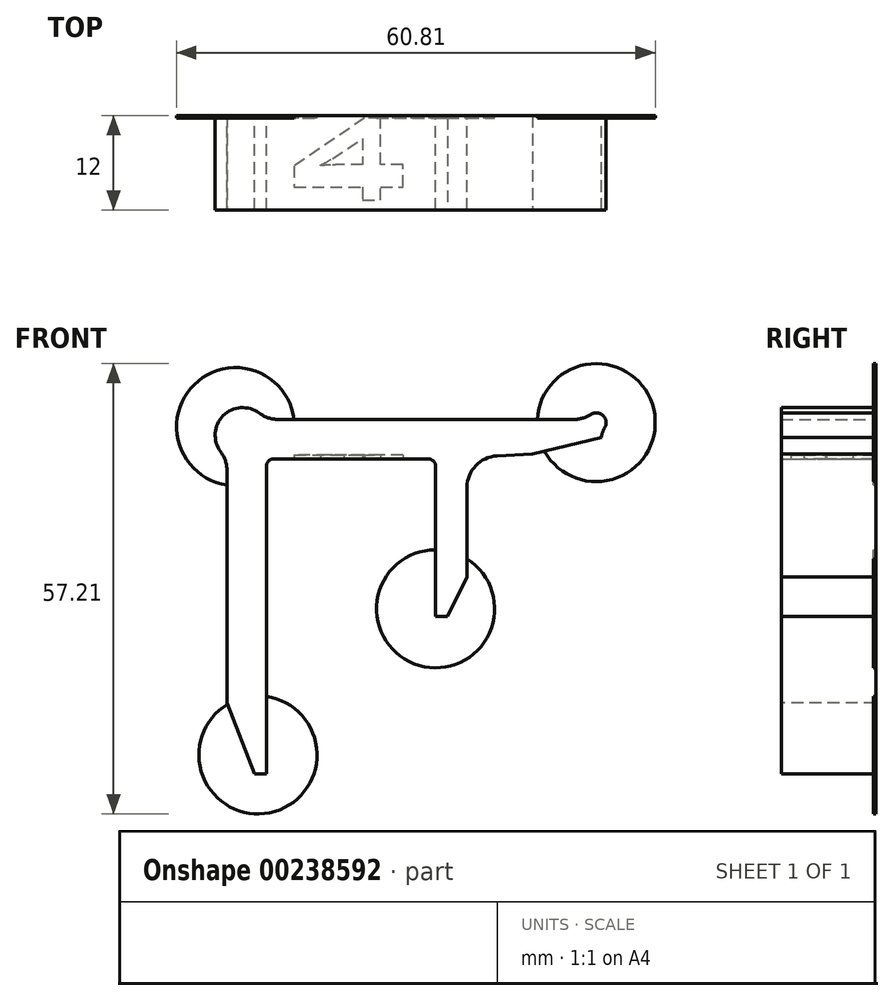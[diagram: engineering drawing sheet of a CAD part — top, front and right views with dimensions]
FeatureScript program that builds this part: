
annotation { "Feature Type Name" : "Feature", "Feature Type Description" : "" }
export const myFeature = defineFeature(function(context is Context, id is Id, definition is map)
    precondition{}
    {
        {
            var Q0;
            Q0=qCreatedBy(makeId("Front.planeOp"),FACE);
            var sketch = newSketch(context, id + "F0", { "sketchPlane" : qUnion([Q0])});
            skLineSegment(sketch, "E0", {"start": v(0, 0) * mm, "end": v(21.5, 0) * mm});
            skLineSegment(sketch, "E1", {"start": v(0, 0) * mm, "end": v(0, -40) * mm});
            skLineSegment(sketch, "E2", {"start": v(0, -40) * mm, "end": v(-5, -40) * mm});
            skLineSegment(sketch, "E3", {"start": v(-5, -40) * mm, "end": v(-5, 5) * mm});
            skLineSegment(sketch, "E4", {"start": v(-5, 5) * mm, "end": v(21.5, 5) * mm});
            skLineSegment(sketch, "E5", {"start": v(21.5, 5) * mm, "end": v(21.5, 0) * mm});
            skLineSegment(sketch, "E6", {"start": v(21.5, 0) * mm, "end": v(42.5, 1) * mm});
            skLineSegment(sketch, "E7", {"start": v(21.5, 0) * mm, "end": v(21.5, -20) * mm});
            skLineSegment(sketch, "E8", {"start": v(21.5, -20) * mm, "end": v(25.5, -20) * mm});
            skLineSegment(sketch, "E9", {"start": v(25.5, -20) * mm, "end": v(25.5, 0.2) * mm});
            skLineSegment(sketch, "E10", {"start": v(21.5, 5) * mm, "end": v(42.5, 5) * mm});
            skLineSegment(sketch, "E11", {"start": v(42.5, 5) * mm, "end": v(42.5, 1) * mm});
            skCircle(sketch, "E12", {"center": v(41.9, 4.6) * mm, "radius": 1.25 * mm});
            skCircle(sketch, "E13", {"center": v(-3, 3) * mm, "radius": 3.5 * mm});
            skSolve(sketch);
        }
        {
            var Q0;
            {var subQ0=sQuery(id+"F0.wireOp",EDGE,"E11");var subQ1=sQuery(id+"F0.wireOp",EDGE,"E10");var subQ2=makeQuery(id+"F0.imprint","INTERSECT",VERTEX,{"derivedFrom":[subQ1,subQ0]});Q0=makeQuery(id+"F0.imprint","IMPRINT",FACE,{"disambiguationData":[TD([[makeQuery(id+"F0.imprint","IMPRINT",EDGE,{"disambiguationData":[TD([[subQ2,1.0]])],"derivedFrom":subQ1}),-1.0]])]});}
            var Q1;
            {var subQ0=sQuery(id+"F0.wireOp",EDGE,"E11");var subQ1=sQuery(id+"F0.wireOp",EDGE,"E10");var subQ2=makeQuery(id+"F0.imprint","INTERSECT",VERTEX,{"derivedFrom":[subQ1,subQ0]});Q1=makeQuery(id+"F0.imprint","IMPRINT",FACE,{"disambiguationData":[TD([[makeQuery(id+"F0.imprint","IMPRINT",EDGE,{"disambiguationData":[TD([[subQ2,1.0]])],"derivedFrom":subQ1}),1.0]])]});}
            var Q2;
            {var subQ1=sQuery(id+"F0.wireOp",EDGE,"E5");Q2=makeQuery(id+"F0.imprint","IMPRINT",FACE,{"disambiguationData":[TD([[makeQuery(id+"F0.imprint","IMPRINT",EDGE,{"derivedFrom":subQ1}),1.0]])]});}
            var Q3;
            {var subQ0=sQuery(id+"F0.wireOp",EDGE,"E7");Q3=makeQuery(id+"F0.imprint","IMPRINT",FACE,{"disambiguationData":[TD([[makeQuery(id+"F0.imprint","IMPRINT",EDGE,{"derivedFrom":subQ0}),1.0]])]});}
            var Q4;
            Q4=makeQuery(id+"F0.imprint","IMPRINT",FACE,{"disambiguationData":[TD([[makeQuery(id+"F0.imprint","IMPRINT",EDGE,{"derivedFrom":sQuery(id+"F0.wireOp",EDGE,"E0")}),1.0]])]});
            var Q5;
            {var subQ0=sQuery(id+"F0.wireOp",EDGE,"E4");var subQ1=sQuery(id+"F0.wireOp",EDGE,"E3");var subQ2=makeQuery(id+"F0.imprint","INTERSECT",VERTEX,{"derivedFrom":[subQ1,subQ0]});Q5=makeQuery(id+"F0.imprint","IMPRINT",FACE,{"disambiguationData":[TD([[makeQuery(id+"F0.imprint","IMPRINT",EDGE,{"disambiguationData":[TD([[subQ2,1.0]])],"derivedFrom":subQ1}),-1.0]])]});}
            var Q6;
            {var subQ0=sQuery(id+"F0.wireOp",EDGE,"E4");var subQ1=sQuery(id+"F0.wireOp",EDGE,"E3");var subQ2=makeQuery(id+"F0.imprint","INTERSECT",VERTEX,{"derivedFrom":[subQ1,subQ0]});Q6=makeQuery(id+"F0.imprint","IMPRINT",FACE,{"disambiguationData":[TD([[makeQuery(id+"F0.imprint","IMPRINT",EDGE,{"disambiguationData":[TD([[subQ2,1.0]])],"derivedFrom":subQ1}),1.0]])]});}
            extrude(context, id + "F1", {"entities" : qUnion([Q0, Q1, Q2, Q3, Q4, Q5, Q6]), "depth" : 12 * mm, "offsetDistance" : 25 * mm, "symmetric" : true});
        }
        {
            var Q0;
            Q0=makeQuery(id+"F1.opExtrude","SWEPT_EDGE",EDGE,{"disambiguationData":[OSD([sQuery(id+"F0.wireOp",EDGE,"E0"),sQuery(id+"F0.wireOp",EDGE,"E1")])]});
            var Q1;
            Q1=makeQuery(id+"F1.opExtrude","SWEPT_EDGE",EDGE,{"disambiguationData":[OSD([sQuery(id+"F0.wireOp",EDGE,"E0"),sQuery(id+"F0.wireOp",EDGE,"E5"),sQuery(id+"F0.wireOp",EDGE,"E6"),sQuery(id+"F0.wireOp",EDGE,"E7")])]});
            fillet(context, id + "F2", {"entities" : qUnion([Q0, Q1]), "radius" : 1 * mm, "tangentPropagation" : true, "allowEdgeOverflow" : false});
        }
        {
            var Q0;
            Q0=makeQuery(id+"F1.opExtrude","SWEPT_EDGE",EDGE,{"disambiguationData":[OSD([sQuery(id+"F0.wireOp",EDGE,"E8"),sQuery(id+"F0.wireOp",EDGE,"E9")])]});
            chamfer(context, id + "F3", {"entities" : qUnion([Q0]), "chamferType" : ChamferType.TWO_OFFSETS, "width1" : 5 * mm, "oppositeDirection" : false, "width2" : 2.5 * mm, "tangentPropagation" : true});
        }
        {
            var Q0;
            Q0=makeQuery(id+"F1.opExtrude","SWEPT_EDGE",EDGE,{"disambiguationData":[OSD([sQuery(id+"F0.wireOp",EDGE,"E6"),sQuery(id+"F0.wireOp",EDGE,"E9")])]});
            var Q1;
            Q1=makeQuery(id+"F1.opExtrude","SWEPT_EDGE",EDGE,{"disambiguationData":[OSD([sQuery(id+"F0.wireOp",EDGE,"E4"),sQuery(id+"F0.wireOp",EDGE,"E13")])]});
            var Q2;
            Q2=makeQuery(id+"F1.opExtrude","SWEPT_EDGE",EDGE,{"disambiguationData":[OSD([sQuery(id+"F0.wireOp",EDGE,"E3"),sQuery(id+"F0.wireOp",EDGE,"E13")])]});
            var Q3;
            Q3=makeQuery(id+"F1.opExtrude","SWEPT_EDGE",EDGE,{"disambiguationData":[OSD([sQuery(id+"F0.wireOp",EDGE,"E10"),sQuery(id+"F0.wireOp",EDGE,"E12")])]});
            var Q4;
            Q4=makeQuery(id+"F1.opExtrude","SWEPT_EDGE",EDGE,{"disambiguationData":[OSD([sQuery(id+"F0.wireOp",EDGE,"E11"),sQuery(id+"F0.wireOp",EDGE,"E12")])]});
            fillet(context, id + "F4", {"entities" : qUnion([Q0, Q1, Q2, Q3, Q4]), "radius" : 4 * mm, "tangentPropagation" : true, "allowEdgeOverflow" : false});
        }
        {
            var Q0;
            Q0=makeQuery(id+"F1.opExtrude","SWEPT_EDGE",EDGE,{"disambiguationData":[OSD([sQuery(id+"F0.wireOp",EDGE,"E2"),sQuery(id+"F0.wireOp",EDGE,"E3")])]});
            var Q1;
            Q1=makeQuery(id+"F1.opExtrude","SWEPT_EDGE",EDGE,{"disambiguationData":[OSD([sQuery(id+"F0.wireOp",EDGE,"E6"),sQuery(id+"F0.wireOp",EDGE,"E11")])]});
            chamfer(context, id + "F5", {"entities" : qUnion([Q0, Q1]), "chamferType" : ChamferType.TWO_OFFSETS, "width1" : 3.5 * mm, "oppositeDirection" : false, "width2" : 9 * mm, "tangentPropagation" : true});
        }
        {
            var Q0;
            Q0=makeQuery(id+"F1.opExtrude","SWEPT_FACE",FACE,{"disambiguationData":[OSD([sQuery(id+"F0.wireOp",EDGE,"E0")])]});
            var sketch = newSketch(context, id + "F6", { "sketchPlane" : qUnion([Q0])});
            skText(sketch, "E14", { "text": "4", "fontName": "OpenSans-Bold.ttf"});
            const initialGuessF6  = {"E14": [0.01736, -0.006, 0, 1, 0.01394]};
            skSetInitialGuess(sketch, initialGuessF6);
            skSolve(sketch);
        }
        {
            var Q0;
            Q0 = qSketchRegion(id + "F6", true);
            extrude(context, id + "F7", {"entities" : qUnion([Q0]), "operationType" : NewBodyOperationType.REMOVE, "oppositeDirection" : true, "depth" : 0.5 * mm, "offsetDistance" : 25 * mm});
        }
        {
            var Q0;
            Q0=makeQuery(id+"F1.opExtrude","CAP_FACE",FACE,{"disambiguationData":[OSD([sQuery(id+"F0.wireOp",EDGE,"E0"),sQuery(id+"F0.wireOp",EDGE,"E1"),sQuery(id+"F0.wireOp",EDGE,"E2"),sQuery(id+"F0.wireOp",EDGE,"E3"),sQuery(id+"F0.wireOp",EDGE,"E4"),sQuery(id+"F0.wireOp",EDGE,"E6"),sQuery(id+"F0.wireOp",EDGE,"E7"),sQuery(id+"F0.wireOp",EDGE,"E8"),sQuery(id+"F0.wireOp",EDGE,"E9"),sQuery(id+"F0.wireOp",EDGE,"E10"),sQuery(id+"F0.wireOp",EDGE,"E11"),sQuery(id+"F0.wireOp",EDGE,"E12"),sQuery(id+"F0.wireOp",EDGE,"E13")])],"isStart":true});
            var sketch = newSketch(context, id + "F8", { "sketchPlane" : qUnion([Q0])});
            skCircle(sketch, "E15", {"center": v(1.06, -37.61) * mm, "radius": 7.5 * mm});
            skCircle(sketch, "E16", {"center": v(-21.5, -19.06) * mm, "radius": 7.5 * mm});
            skCircle(sketch, "E17", {"center": v(-41.9, 4.6) * mm, "radius": 7.5 * mm});
            skCircle(sketch, "E18", {"center": v(3.9, 4.08) * mm, "radius": 7.5 * mm});
            skSolve(sketch);
        }
        {
            var Q0;
            {var subQ0=sQuery(id+"F0.wireOp",EDGE,"E12");Q0=makeQuery(id+"F8.imprint","IMPRINT",FACE,{"disambiguationData":[TD([[makeQuery(id+"F8.imprint","IMPRINT",EDGE,{"derivedFrom":makeQuery(id+"F1.opExtrude","CAP_EDGE",EDGE,{"disambiguationData":[OSD([subQ0])],"isStart":true})}),1.0]])]});}
            var Q1;
            {var subQ0=sQuery(id+"F0.wireOp",EDGE,"E13");Q1=makeQuery(id+"F8.imprint","IMPRINT",FACE,{"disambiguationData":[TD([[makeQuery(id+"F8.imprint","IMPRINT",EDGE,{"derivedFrom":makeQuery(id+"F1.opExtrude","CAP_EDGE",EDGE,{"disambiguationData":[OSD([subQ0])],"isStart":true})}),1.0]])]});}
            var Q2;
            {var subQ5=sQuery(id+"F0.wireOp",EDGE,"E8");var subQ8=makeQuery(id+"F1.opExtrude","CAP_EDGE",EDGE,{"disambiguationData":[OSD([subQ5])],"isStart":true});Q2=makeQuery(id+"F8.imprint","IMPRINT",FACE,{"disambiguationData":[TD([[makeQuery(id+"F8.imprint","IMPRINT",EDGE,{"derivedFrom":subQ8}),1.0]])]});}
            var Q3;
            {var subQ5=sQuery(id+"F0.wireOp",EDGE,"E2");var subQ8=makeQuery(id+"F1.opExtrude","CAP_EDGE",EDGE,{"disambiguationData":[OSD([subQ5])],"isStart":true});Q3=makeQuery(id+"F8.imprint","IMPRINT",FACE,{"disambiguationData":[TD([[makeQuery(id+"F8.imprint","IMPRINT",EDGE,{"derivedFrom":subQ8}),-1.0]])]});}
            extrude(context, id + "F9", {"entities" : qUnion([Q0, Q1, Q2, Q3]), "operationType" : NewBodyOperationType.ADD, "oppositeDirection" : true, "depth" : 0.3 * mm, "offsetDistance" : 25 * mm});
        }
    });
